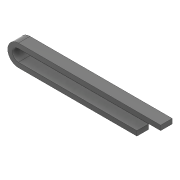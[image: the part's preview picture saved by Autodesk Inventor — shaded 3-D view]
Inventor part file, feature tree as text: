
AUTODESK INVENTOR PART (.ipt)
format: ipt  version: 2020 (Build 240168000, 168)  size: 97,280 bytes
history: native  units: mm
features: extrude x1, sketch x1
ambient origin geometry x8: Origin, YZ Plane, XZ Plane, XY Plane, X Axis, Y Axis, Z Axis, Center Point
bodies: Solid1 (feature_tree)
feature tree (2):
  extrude  "Extrusion1"  Depth=20.0mm
  sketch  "Sketch1"  dims[d0=90.0mm d1=20.0mm d2=20.0mm d4=500.0mm d5=49.0mm d6=0.0mm d9=600.0mm]
